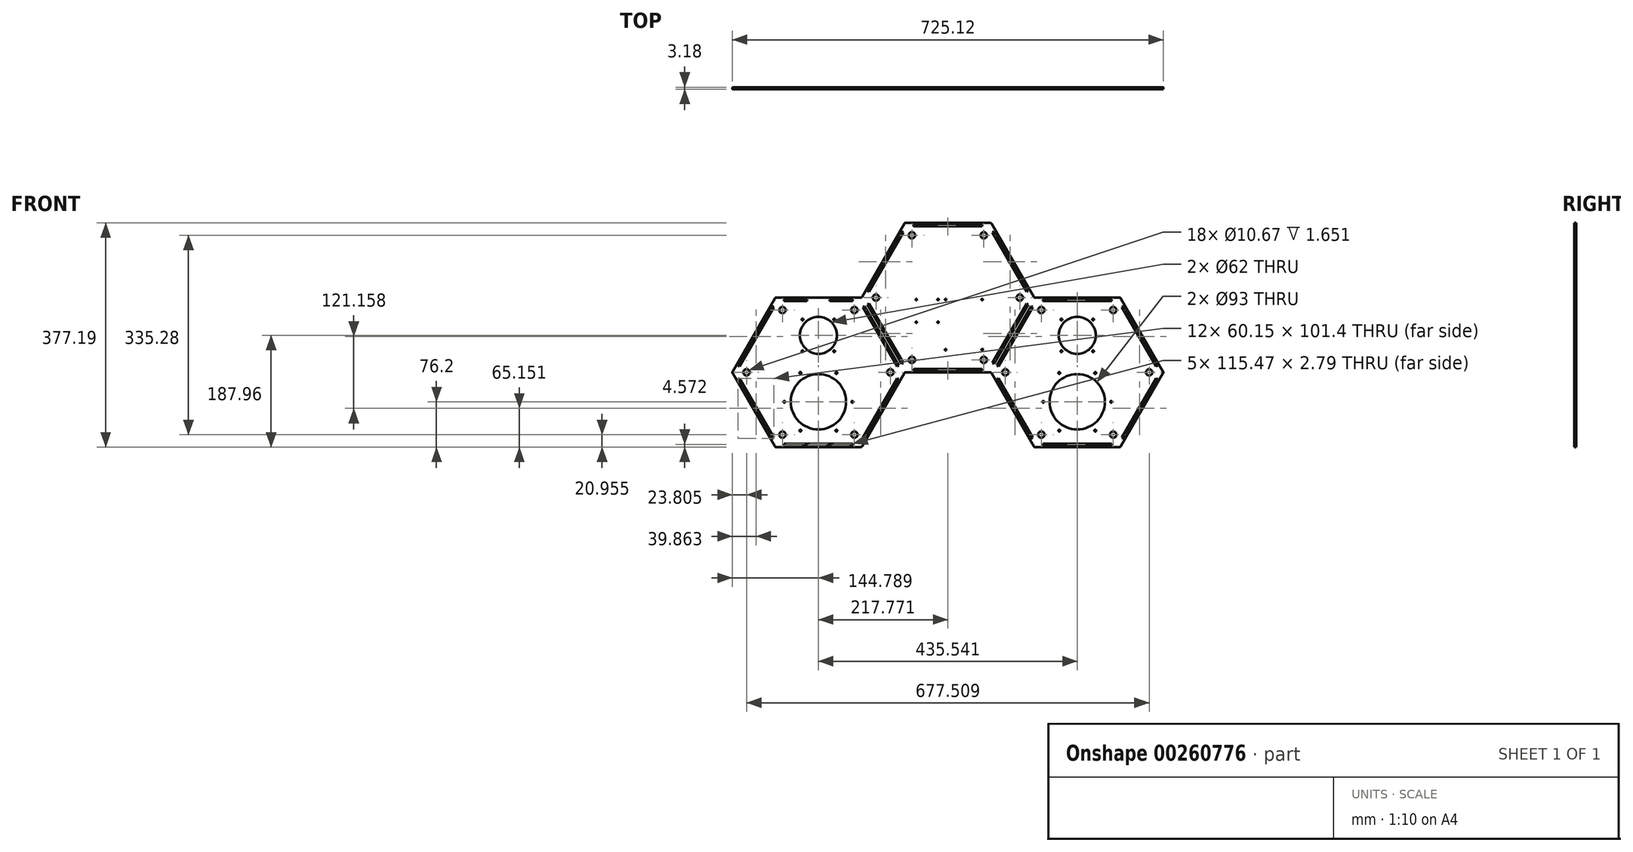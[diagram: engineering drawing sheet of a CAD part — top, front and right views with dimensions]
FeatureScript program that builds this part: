
annotation { "Feature Type Name" : "Feature", "Feature Type Description" : "" }
export const myFeature = defineFeature(function(context is Context, id is Id, definition is map)
    precondition{}
    {
        {
            var Q0;
            Q0=qCreatedBy(makeId("Front.planeOp"),FACE);
            var sketch = newSketch(context, id + "F0", { "sketchPlane" : qUnion([Q0])});
            skCircle(sketch, "E0.cCircle", {"center": v(0, 0) * mm, "radius": 125.73 * mm, "construction": true});
            skLineSegment(sketch, "E0.1", {"start": v(71.12, -125.73) * mm, "end": v(-71.12, -125.73) * mm});
            skLineSegment(sketch, "E0.3", {"start": v(-144.45, 1.27) * mm, "end": v(-73.32, 124.46) * mm});
            skLineSegment(sketch, "E0.4", {"start": v(-71.12, 125.73) * mm, "end": v(71.12, 125.73) * mm});
            skLineSegment(sketch, "E0.5", {"start": v(73.32, 124.46) * mm, "end": v(144.45, 1.27) * mm});
            skCircle(sketch, "E1.cCircle", {"center": v(-217.77, -125.73) * mm, "radius": 125.73 * mm, "construction": true});
            skLineSegment(sketch, "E1.0", {"start": v(-146.65, -251.46) * mm, "end": v(-288.9, -251.46) * mm});
            skLineSegment(sketch, "E1.1", {"start": v(-291.1, -250.19) * mm, "end": v(-362.22, -127) * mm});
            skLineSegment(sketch, "E1.2", {"start": v(-362.22, -124.46) * mm, "end": v(-291.1, -1.27) * mm});
            skLineSegment(sketch, "E1.3", {"start": v(-288.9, 0) * mm, "end": v(-146.65, 0) * mm});
            skLineSegment(sketch, "E1.5", {"start": v(-73.32, -127) * mm, "end": v(-144.45, -250.19) * mm});
            skPoint(sketch, "E1.0.midPoint", {"position": v(-217.77, -251.46) * mm});
            skCircle(sketch, "E2.cCircle", {"center": v(217.77, -125.73) * mm, "radius": 125.73 * mm, "construction": true});
            skLineSegment(sketch, "E2.0", {"start": v(362.22, -127) * mm, "end": v(291.1, -250.2) * mm});
            skLineSegment(sketch, "E2.1", {"start": v(288.9, -251.46) * mm, "end": v(146.65, -251.46) * mm});
            skLineSegment(sketch, "E2.2", {"start": v(144.45, -250.2) * mm, "end": v(73.32, -127) * mm});
            skLineSegment(sketch, "E2.4", {"start": v(146.65, 0) * mm, "end": v(288.9, 0) * mm});
            skLineSegment(sketch, "E2.5", {"start": v(291.1, -1.27) * mm, "end": v(362.22, -124.46) * mm});
            skPoint(sketch, "E2.0.midPoint", {"position": v(326.66, -188.6) * mm});
            skPoint(sketch, "E3.visualSharp", {"position": v(-72.6, 125.73) * mm});
            skArc(sketch, "E3.filletArc", {"start": v(-71.12, 125.73) * mm, "mid": v(-72.4, 125.39) * mm, "end": v(-73.32, 124.46) * mm});
            skPoint(sketch, "E4.visualSharp", {"position": v(72.6, 125.73) * mm});
            skArc(sketch, "E4.filletArc", {"start": v(73.32, 124.46) * mm, "mid": v(72.4, 125.39) * mm, "end": v(71.12, 125.73) * mm});
            skPoint(sketch, "E5.visualSharp", {"position": v(145.18, 0) * mm});
            skArc(sketch, "E5.filletArc", {"start": v(144.45, 1.27) * mm, "mid": v(145.38, 0.34) * mm, "end": v(146.65, 0) * mm});
            skPoint(sketch, "E6.visualSharp", {"position": v(290.36, 0) * mm});
            skArc(sketch, "E6.filletArc", {"start": v(291.1, -1.27) * mm, "mid": v(290.16, -0.34) * mm, "end": v(288.9, 0) * mm});
            skPoint(sketch, "E7.visualSharp", {"position": v(362.95, -125.73) * mm});
            skArc(sketch, "E7.filletArc", {"start": v(362.22, -127) * mm, "mid": v(362.56, -125.73) * mm, "end": v(362.22, -124.46) * mm});
            skPoint(sketch, "E8.visualSharp", {"position": v(290.36, -251.46) * mm});
            skArc(sketch, "E8.filletArc", {"start": v(288.9, -251.46) * mm, "mid": v(290.16, -251.12) * mm, "end": v(291.1, -250.2) * mm});
            skPoint(sketch, "E9.visualSharp", {"position": v(145.18, -251.46) * mm});
            skArc(sketch, "E9.filletArc", {"start": v(144.45, -250.2) * mm, "mid": v(145.38, -251.12) * mm, "end": v(146.65, -251.46) * mm});
            skPoint(sketch, "E10.visualSharp", {"position": v(72.6, -125.73) * mm});
            skArc(sketch, "E10.filletArc", {"start": v(73.32, -127) * mm, "mid": v(72.4, -126.07) * mm, "end": v(71.12, -125.73) * mm});
            skPoint(sketch, "E11.visualSharp", {"position": v(-72.6, -125.73) * mm});
            skArc(sketch, "E11.filletArc", {"start": v(-71.12, -125.73) * mm, "mid": v(-72.4, -126.07) * mm, "end": v(-73.32, -127) * mm});
            skPoint(sketch, "E12.visualSharp", {"position": v(-145.18, -251.46) * mm});
            skArc(sketch, "E12.filletArc", {"start": v(-146.65, -251.46) * mm, "mid": v(-145.38, -251.12) * mm, "end": v(-144.45, -250.19) * mm});
            skPoint(sketch, "E13.visualSharp", {"position": v(-290.36, -251.46) * mm});
            skArc(sketch, "E13.filletArc", {"start": v(-291.1, -250.19) * mm, "mid": v(-290.16, -251.12) * mm, "end": v(-288.9, -251.46) * mm});
            skPoint(sketch, "E14.visualSharp", {"position": v(-362.95, -125.73) * mm});
            skArc(sketch, "E14.filletArc", {"start": v(-362.22, -124.46) * mm, "mid": v(-362.56, -125.73) * mm, "end": v(-362.22, -127) * mm});
            skPoint(sketch, "E15.visualSharp", {"position": v(-290.36, 0) * mm});
            skArc(sketch, "E15.filletArc", {"start": v(-288.9, 0) * mm, "mid": v(-290.16, -0.34) * mm, "end": v(-291.1, -1.27) * mm});
            skPoint(sketch, "E16.visualSharp", {"position": v(-145.18, 0) * mm});
            skArc(sketch, "E16.filletArc", {"start": v(-146.65, 0) * mm, "mid": v(-145.38, 0.34) * mm, "end": v(-144.45, 1.27) * mm});
            skCircle(sketch, "E17.cCircle", {"center": v(-217.77, -125.73) * mm, "radius": 104.78 * mm, "construction": true});
            skLineSegment(sketch, "E17.0", {"start": v(-278.26, -20.95) * mm, "end": v(-157.28, -20.96) * mm, "construction": true});
            skLineSegment(sketch, "E17.1", {"start": v(-157.28, -20.95) * mm, "end": v(-96.79, -125.73) * mm, "construction": true});
            skLineSegment(sketch, "E17.2", {"start": v(-96.79, -125.73) * mm, "end": v(-157.28, -230.5) * mm, "construction": true});
            skLineSegment(sketch, "E17.3", {"start": v(-157.28, -230.5) * mm, "end": v(-278.26, -230.5) * mm, "construction": true});
            skLineSegment(sketch, "E17.4", {"start": v(-278.26, -230.5) * mm, "end": v(-338.75, -125.73) * mm, "construction": true});
            skLineSegment(sketch, "E17.5", {"start": v(-338.75, -125.73) * mm, "end": v(-278.26, -20.96) * mm, "construction": true});
            skPoint(sketch, "E17.0.midPoint", {"position": v(-217.77, -20.96) * mm});
            skCircle(sketch, "E18.cCircle", {"center": v(0, 0) * mm, "radius": 104.78 * mm, "construction": true});
            skLineSegment(sketch, "E18.0", {"start": v(60.5, 104.78) * mm, "end": v(120.98, 0) * mm, "construction": true});
            skLineSegment(sketch, "E18.1", {"start": v(120.98, 0) * mm, "end": v(60.5, -104.77) * mm, "construction": true});
            skLineSegment(sketch, "E18.2", {"start": v(60.5, -104.77) * mm, "end": v(-60.5, -104.78) * mm, "construction": true});
            skLineSegment(sketch, "E18.3", {"start": v(-60.5, -104.78) * mm, "end": v(-120.98, 0) * mm, "construction": true});
            skLineSegment(sketch, "E18.4", {"start": v(-120.98, 0) * mm, "end": v(-60.5, 104.78) * mm, "construction": true});
            skLineSegment(sketch, "E18.5", {"start": v(-60.5, 104.77) * mm, "end": v(60.5, 104.77) * mm, "construction": true});
            skPoint(sketch, "E18.0.midPoint", {"position": v(90.74, 52.39) * mm});
            skCircle(sketch, "E19.cCircle", {"center": v(217.77, -125.73) * mm, "radius": 104.78 * mm, "construction": true});
            skLineSegment(sketch, "E19.0", {"start": v(157.28, -20.96) * mm, "end": v(278.26, -20.96) * mm, "construction": true});
            skLineSegment(sketch, "E19.1", {"start": v(278.26, -20.96) * mm, "end": v(338.75, -125.73) * mm, "construction": true});
            skLineSegment(sketch, "E19.2", {"start": v(338.75, -125.73) * mm, "end": v(278.26, -230.5) * mm, "construction": true});
            skLineSegment(sketch, "E19.3", {"start": v(278.26, -230.5) * mm, "end": v(157.28, -230.5) * mm, "construction": true});
            skLineSegment(sketch, "E19.4", {"start": v(157.28, -230.5) * mm, "end": v(96.79, -125.73) * mm, "construction": true});
            skLineSegment(sketch, "E19.5", {"start": v(96.79, -125.73) * mm, "end": v(157.28, -20.96) * mm, "construction": true});
            skPoint(sketch, "E19.0.midPoint", {"position": v(217.77, -20.96) * mm});
            skCircle(sketch, "E20", {"center": v(-278.26, -20.96) * mm, "radius": 5.33 * mm});
            skCircle(sketch, "E21", {"center": v(-157.28, -20.95) * mm, "radius": 5.33 * mm});
            skCircle(sketch, "E22", {"center": v(-338.75, -125.73) * mm, "radius": 5.33 * mm});
            skCircle(sketch, "E23", {"center": v(-278.26, -230.5) * mm, "radius": 5.33 * mm});
            skCircle(sketch, "E24", {"center": v(-157.28, -230.5) * mm, "radius": 5.33 * mm});
            skCircle(sketch, "E25", {"center": v(-96.79, -125.73) * mm, "radius": 5.33 * mm});
            skCircle(sketch, "E26", {"center": v(-60.5, -104.78) * mm, "radius": 5.33 * mm});
            skCircle(sketch, "E27", {"center": v(-120.98, 0) * mm, "radius": 5.33 * mm});
            skCircle(sketch, "E28", {"center": v(-60.5, 104.77) * mm, "radius": 5.33 * mm});
            skCircle(sketch, "E29", {"center": v(60.5, 104.77) * mm, "radius": 5.33 * mm});
            skCircle(sketch, "E30", {"center": v(120.98, 0) * mm, "radius": 5.33 * mm});
            skCircle(sketch, "E31", {"center": v(60.5, -104.77) * mm, "radius": 5.33 * mm});
            skCircle(sketch, "E32", {"center": v(96.79, -125.73) * mm, "radius": 5.33 * mm});
            skCircle(sketch, "E33", {"center": v(157.28, -20.96) * mm, "radius": 5.33 * mm});
            skCircle(sketch, "E34", {"center": v(278.26, -20.96) * mm, "radius": 5.33 * mm});
            skCircle(sketch, "E35", {"center": v(338.75, -125.73) * mm, "radius": 5.33 * mm});
            skCircle(sketch, "E36", {"center": v(278.26, -230.5) * mm, "radius": 5.33 * mm});
            skCircle(sketch, "E37", {"center": v(157.28, -230.5) * mm, "radius": 5.33 * mm});
            skSolve(sketch);
        }
        {
            var Q0;
            Q0=makeQuery(id+"F0.imprint","IMPRINT",FACE,{"disambiguationData":[TD([[makeQuery(id+"F0.imprint","IMPRINT",EDGE,{"derivedFrom":sQuery(id+"F0.wireOp",EDGE,"E0.1")}),-1.0]])]});
            extrude(context, id + "F1", {"entities" : qUnion([Q0]), "depth" : 3.17 * mm});
        }
        {
            var Q0;
            Q0=makeQuery(id+"F0.imprint","IMPRINT",FACE,{"disambiguationData":[TD([[makeQuery(id+"F0.imprint","IMPRINT",EDGE,{"derivedFrom":sQuery(id+"F0.wireOp",EDGE,"E30")}),1.0]])]});
            var Q1;
            Q1=makeQuery(id+"F0.imprint","IMPRINT",FACE,{"disambiguationData":[TD([[makeQuery(id+"F0.imprint","IMPRINT",EDGE,{"derivedFrom":sQuery(id+"F0.wireOp",EDGE,"E33")}),1.0]])]});
            var Q2;
            Q2=makeQuery(id+"F0.imprint","IMPRINT",FACE,{"disambiguationData":[TD([[makeQuery(id+"F0.imprint","IMPRINT",EDGE,{"derivedFrom":sQuery(id+"F0.wireOp",EDGE,"E34")}),1.0]])]});
            var Q3;
            Q3=makeQuery(id+"F0.imprint","IMPRINT",FACE,{"disambiguationData":[TD([[makeQuery(id+"F0.imprint","IMPRINT",EDGE,{"derivedFrom":sQuery(id+"F0.wireOp",EDGE,"E35")}),1.0]])]});
            var Q4;
            Q4=makeQuery(id+"F0.imprint","IMPRINT",FACE,{"disambiguationData":[TD([[makeQuery(id+"F0.imprint","IMPRINT",EDGE,{"derivedFrom":sQuery(id+"F0.wireOp",EDGE,"E36")}),1.0]])]});
            var Q5;
            Q5=makeQuery(id+"F0.imprint","IMPRINT",FACE,{"disambiguationData":[TD([[makeQuery(id+"F0.imprint","IMPRINT",EDGE,{"derivedFrom":sQuery(id+"F0.wireOp",EDGE,"E37")}),1.0]])]});
            var Q6;
            Q6=makeQuery(id+"F0.imprint","IMPRINT",FACE,{"disambiguationData":[TD([[makeQuery(id+"F0.imprint","IMPRINT",EDGE,{"derivedFrom":sQuery(id+"F0.wireOp",EDGE,"E32")}),1.0]])]});
            var Q7;
            Q7=makeQuery(id+"F0.imprint","IMPRINT",FACE,{"disambiguationData":[TD([[makeQuery(id+"F0.imprint","IMPRINT",EDGE,{"derivedFrom":sQuery(id+"F0.wireOp",EDGE,"E31")}),1.0]])]});
            var Q8;
            Q8=makeQuery(id+"F0.imprint","IMPRINT",FACE,{"disambiguationData":[TD([[makeQuery(id+"F0.imprint","IMPRINT",EDGE,{"derivedFrom":sQuery(id+"F0.wireOp",EDGE,"E26")}),1.0]])]});
            var Q9;
            Q9=makeQuery(id+"F0.imprint","IMPRINT",FACE,{"disambiguationData":[TD([[makeQuery(id+"F0.imprint","IMPRINT",EDGE,{"derivedFrom":sQuery(id+"F0.wireOp",EDGE,"E25")}),1.0]])]});
            var Q10;
            Q10=makeQuery(id+"F0.imprint","IMPRINT",FACE,{"disambiguationData":[TD([[makeQuery(id+"F0.imprint","IMPRINT",EDGE,{"derivedFrom":sQuery(id+"F0.wireOp",EDGE,"E24")}),1.0]])]});
            var Q11;
            Q11=makeQuery(id+"F0.imprint","IMPRINT",FACE,{"disambiguationData":[TD([[makeQuery(id+"F0.imprint","IMPRINT",EDGE,{"derivedFrom":sQuery(id+"F0.wireOp",EDGE,"E23")}),1.0]])]});
            var Q12;
            Q12=makeQuery(id+"F0.imprint","IMPRINT",FACE,{"disambiguationData":[TD([[makeQuery(id+"F0.imprint","IMPRINT",EDGE,{"derivedFrom":sQuery(id+"F0.wireOp",EDGE,"E22")}),1.0]])]});
            var Q13;
            Q13=makeQuery(id+"F0.imprint","IMPRINT",FACE,{"disambiguationData":[TD([[makeQuery(id+"F0.imprint","IMPRINT",EDGE,{"derivedFrom":sQuery(id+"F0.wireOp",EDGE,"E20")}),1.0]])]});
            var Q14;
            Q14=makeQuery(id+"F0.imprint","IMPRINT",FACE,{"disambiguationData":[TD([[makeQuery(id+"F0.imprint","IMPRINT",EDGE,{"derivedFrom":sQuery(id+"F0.wireOp",EDGE,"E21")}),1.0]])]});
            var Q15;
            Q15=makeQuery(id+"F0.imprint","IMPRINT",FACE,{"disambiguationData":[TD([[makeQuery(id+"F0.imprint","IMPRINT",EDGE,{"derivedFrom":sQuery(id+"F0.wireOp",EDGE,"E27")}),1.0]])]});
            var Q16;
            Q16=makeQuery(id+"F0.imprint","IMPRINT",FACE,{"disambiguationData":[TD([[makeQuery(id+"F0.imprint","IMPRINT",EDGE,{"derivedFrom":sQuery(id+"F0.wireOp",EDGE,"E28")}),1.0]])]});
            var Q17;
            Q17=makeQuery(id+"F0.imprint","IMPRINT",FACE,{"disambiguationData":[TD([[makeQuery(id+"F0.imprint","IMPRINT",EDGE,{"derivedFrom":sQuery(id+"F0.wireOp",EDGE,"E29")}),1.0]])]});
            extrude(context, id + "F2", {"entities" : qUnion([Q0, Q1, Q2, Q3, Q4, Q5, Q6, Q7, Q8, Q9, Q10, Q11, Q12, Q13, Q14, Q15, Q16, Q17]), "operationType" : NewBodyOperationType.ADD, "depth" : 1.52 * mm});
        }
        {
            var Q0;
            Q0=makeQuery(id+"F1.opExtrude","CAP_FACE",FACE,{"disambiguationData":[OSD([sQuery(id+"F0.wireOp",EDGE,"E0.1"),sQuery(id+"F0.wireOp",EDGE,"E0.3"),sQuery(id+"F0.wireOp",EDGE,"E0.4"),sQuery(id+"F0.wireOp",EDGE,"E0.5"),sQuery(id+"F0.wireOp",EDGE,"E1.0"),sQuery(id+"F0.wireOp",EDGE,"E1.1"),sQuery(id+"F0.wireOp",EDGE,"E1.2"),sQuery(id+"F0.wireOp",EDGE,"E1.3"),sQuery(id+"F0.wireOp",EDGE,"E1.5"),sQuery(id+"F0.wireOp",EDGE,"E2.0"),sQuery(id+"F0.wireOp",EDGE,"E2.1"),sQuery(id+"F0.wireOp",EDGE,"E2.2"),sQuery(id+"F0.wireOp",EDGE,"E2.4"),sQuery(id+"F0.wireOp",EDGE,"E2.5"),sQuery(id+"F0.wireOp",EDGE,"E3.filletArc"),sQuery(id+"F0.wireOp",EDGE,"E4.filletArc"),sQuery(id+"F0.wireOp",EDGE,"E5.filletArc"),sQuery(id+"F0.wireOp",EDGE,"E6.filletArc"),sQuery(id+"F0.wireOp",EDGE,"E7.filletArc"),sQuery(id+"F0.wireOp",EDGE,"E8.filletArc"),sQuery(id+"F0.wireOp",EDGE,"E9.filletArc"),sQuery(id+"F0.wireOp",EDGE,"E10.filletArc"),sQuery(id+"F0.wireOp",EDGE,"E11.filletArc"),sQuery(id+"F0.wireOp",EDGE,"E12.filletArc"),sQuery(id+"F0.wireOp",EDGE,"E13.filletArc"),sQuery(id+"F0.wireOp",EDGE,"E14.filletArc"),sQuery(id+"F0.wireOp",EDGE,"E15.filletArc"),sQuery(id+"F0.wireOp",EDGE,"E16.filletArc"),sQuery(id+"F0.wireOp",EDGE,"E20"),sQuery(id+"F0.wireOp",EDGE,"E21"),sQuery(id+"F0.wireOp",EDGE,"E22"),sQuery(id+"F0.wireOp",EDGE,"E23"),sQuery(id+"F0.wireOp",EDGE,"E24"),sQuery(id+"F0.wireOp",EDGE,"E25"),sQuery(id+"F0.wireOp",EDGE,"E26"),sQuery(id+"F0.wireOp",EDGE,"E27"),sQuery(id+"F0.wireOp",EDGE,"E28"),sQuery(id+"F0.wireOp",EDGE,"E29"),sQuery(id+"F0.wireOp",EDGE,"E30"),sQuery(id+"F0.wireOp",EDGE,"E31"),sQuery(id+"F0.wireOp",EDGE,"E32"),sQuery(id+"F0.wireOp",EDGE,"E33"),sQuery(id+"F0.wireOp",EDGE,"E34"),sQuery(id+"F0.wireOp",EDGE,"E35"),sQuery(id+"F0.wireOp",EDGE,"E36"),sQuery(id+"F0.wireOp",EDGE,"E37")])],"isStart":false});
            var sketch = newSketch(context, id + "F3", { "sketchPlane" : qUnion([Q0])});
            skPoint(sketch, "E38", {"position": v(-217.77, -127) * mm});
            skCircle(sketch, "E39", {"center": v(-217.77, -63.5) * mm, "radius": 31 * mm});
            skCircle(sketch, "E40", {"center": v(-217.77, -175.26) * mm, "radius": 46.5 * mm});
            skLineSegment(sketch, "E41", {"start": v(-295.75, -175.26) * mm, "end": v(-133.33, -175.26) * mm, "construction": true});
            skCircle(sketch, "E42", {"center": v(-217.77, -175.26) * mm, "radius": 61.65 * mm, "construction": true});
            skCircle(sketch, "E43", {"center": v(-217.77, -175.26) * mm, "radius": 57.15 * mm, "construction": true});
            skCircle(sketch, "E44", {"center": v(-160.62, -175.26) * mm, "radius": 1.52 * mm});
            skLineSegment(sketch, "E45", {"start": v(-217.77, -175.26) * mm, "end": v(-217.77, -149.19) * mm, "construction": true});
            skLineSegment(sketch, "E46", {"start": v(-217.77, -175.26) * mm, "end": v(-187.49, -126.8) * mm, "construction": true});
            skLineSegment(sketch, "E47", {"start": v(-217.77, -175.26) * mm, "end": v(-187.49, -223.73) * mm, "construction": true});
            skCircle(sketch, "E48", {"center": v(-187.49, -126.8) * mm, "radius": 1.52 * mm});
            skCircle(sketch, "E49", {"center": v(-187.49, -223.73) * mm, "radius": 1.52 * mm});
            skCircle(sketch, "E50.MirrorC", {"center": v(-248.06, -126.8) * mm, "radius": 1.52 * mm});
            skCircle(sketch, "E51.MirrorC", {"center": v(-248.06, -223.73) * mm, "radius": 1.52 * mm});
            skCircle(sketch, "E52.MirrorC", {"center": v(-274.92, -175.26) * mm, "radius": 1.52 * mm});
            skCircle(sketch, "E53", {"center": v(-217.77, -63.5) * mm, "radius": 37.72 * mm, "construction": true});
            skLineSegment(sketch, "E54", {"start": v(-217.77, -63.5) * mm, "end": v(-244.44, -36.83) * mm, "construction": true});
            skCircle(sketch, "E55", {"center": v(-244.44, -36.83) * mm, "radius": 1.52 * mm});
            skCircle(sketch, "E56", {"center": v(-244.44, -90.17) * mm, "radius": 1.52 * mm});
            skCircle(sketch, "E57", {"center": v(-191.1, -90.17) * mm, "radius": 1.52 * mm});
            skCircle(sketch, "E58", {"center": v(-191.1, -36.83) * mm, "radius": 1.52 * mm});
            skLineSegment(sketch, "E59", {"start": v(-244.44, -36.83) * mm, "end": v(-191.1, -36.83) * mm, "construction": true});
            skCircle(sketch, "E60.MirrorC", {"center": v(160.62, -175.26) * mm, "radius": 1.52 * mm});
            skCircle(sketch, "E61.MirrorC", {"center": v(187.49, -223.73) * mm, "radius": 1.52 * mm});
            skCircle(sketch, "E62.MirrorC", {"center": v(248.06, -223.73) * mm, "radius": 1.52 * mm});
            skCircle(sketch, "E63.MirrorC", {"center": v(274.92, -175.26) * mm, "radius": 1.52 * mm});
            skCircle(sketch, "E64.MirrorC", {"center": v(187.49, -126.8) * mm, "radius": 1.52 * mm});
            skCircle(sketch, "E65.MirrorC", {"center": v(248.06, -126.8) * mm, "radius": 1.52 * mm});
            skCircle(sketch, "E66.MirrorC", {"center": v(217.77, -175.26) * mm, "radius": 46.5 * mm});
            skCircle(sketch, "E67.MirrorC", {"center": v(244.44, -90.17) * mm, "radius": 1.52 * mm});
            skCircle(sketch, "E68.MirrorC", {"center": v(191.1, -90.17) * mm, "radius": 1.52 * mm});
            skCircle(sketch, "E69.MirrorC", {"center": v(191.1, -36.83) * mm, "radius": 1.52 * mm});
            skCircle(sketch, "E70.MirrorC", {"center": v(217.77, -63.5) * mm, "radius": 31 * mm});
            skCircle(sketch, "E71.MirrorC", {"center": v(244.44, -36.83) * mm, "radius": 1.52 * mm});
            skSolve(sketch);
        }
        {
            var Q0;
            Q0=qSketchRegion(id+"F3",true);
            extrude(context, id + "F4", {"entities" : qUnion([Q0]), "operationType" : NewBodyOperationType.REMOVE, "endBound" : BoundingType.THROUGH_ALL, "oppositeDirection" : true, "depth" : 25.4 * mm});
        }
        {
            var Q0;
            Q0=makeQuery(id+"F1.opExtrude","CAP_FACE",FACE,{"disambiguationData":[OSD([sQuery(id+"F0.wireOp",EDGE,"E0.1"),sQuery(id+"F0.wireOp",EDGE,"E0.3"),sQuery(id+"F0.wireOp",EDGE,"E0.4"),sQuery(id+"F0.wireOp",EDGE,"E0.5"),sQuery(id+"F0.wireOp",EDGE,"E1.0"),sQuery(id+"F0.wireOp",EDGE,"E1.1"),sQuery(id+"F0.wireOp",EDGE,"E1.2"),sQuery(id+"F0.wireOp",EDGE,"E1.3"),sQuery(id+"F0.wireOp",EDGE,"E1.5"),sQuery(id+"F0.wireOp",EDGE,"E2.0"),sQuery(id+"F0.wireOp",EDGE,"E2.1"),sQuery(id+"F0.wireOp",EDGE,"E2.2"),sQuery(id+"F0.wireOp",EDGE,"E2.4"),sQuery(id+"F0.wireOp",EDGE,"E2.5"),sQuery(id+"F0.wireOp",EDGE,"E3.filletArc"),sQuery(id+"F0.wireOp",EDGE,"E4.filletArc"),sQuery(id+"F0.wireOp",EDGE,"E5.filletArc"),sQuery(id+"F0.wireOp",EDGE,"E6.filletArc"),sQuery(id+"F0.wireOp",EDGE,"E7.filletArc"),sQuery(id+"F0.wireOp",EDGE,"E8.filletArc"),sQuery(id+"F0.wireOp",EDGE,"E9.filletArc"),sQuery(id+"F0.wireOp",EDGE,"E10.filletArc"),sQuery(id+"F0.wireOp",EDGE,"E11.filletArc"),sQuery(id+"F0.wireOp",EDGE,"E12.filletArc"),sQuery(id+"F0.wireOp",EDGE,"E13.filletArc"),sQuery(id+"F0.wireOp",EDGE,"E14.filletArc"),sQuery(id+"F0.wireOp",EDGE,"E15.filletArc"),sQuery(id+"F0.wireOp",EDGE,"E16.filletArc"),sQuery(id+"F0.wireOp",EDGE,"E20"),sQuery(id+"F0.wireOp",EDGE,"E21"),sQuery(id+"F0.wireOp",EDGE,"E22"),sQuery(id+"F0.wireOp",EDGE,"E23"),sQuery(id+"F0.wireOp",EDGE,"E24"),sQuery(id+"F0.wireOp",EDGE,"E25"),sQuery(id+"F0.wireOp",EDGE,"E26"),sQuery(id+"F0.wireOp",EDGE,"E27"),sQuery(id+"F0.wireOp",EDGE,"E28"),sQuery(id+"F0.wireOp",EDGE,"E29"),sQuery(id+"F0.wireOp",EDGE,"E30"),sQuery(id+"F0.wireOp",EDGE,"E31"),sQuery(id+"F0.wireOp",EDGE,"E32"),sQuery(id+"F0.wireOp",EDGE,"E33"),sQuery(id+"F0.wireOp",EDGE,"E34"),sQuery(id+"F0.wireOp",EDGE,"E35"),sQuery(id+"F0.wireOp",EDGE,"E36"),sQuery(id+"F0.wireOp",EDGE,"E37")])],"isStart":false});
            var sketch = newSketch(context, id + "F5", { "sketchPlane" : qUnion([Q0])});
            skPoint(sketch, "E72", {"position": v(-217.77, -125.73) * mm});
            skCircle(sketch, "E73.cCircle", {"center": v(-217.77, -125.73) * mm, "radius": 125.73 * mm, "construction": true});
            skLineSegment(sketch, "E73.0", {"start": v(-275.7, 0) * mm, "end": v(-159.85, 0) * mm, "construction": true});
            skLineSegment(sketch, "E73.1", {"start": v(-137.85, -12.7) * mm, "end": v(-79.92, -113.03) * mm, "construction": true});
            skLineSegment(sketch, "E73.2", {"start": v(-79.92, -138.43) * mm, "end": v(-137.85, -238.76) * mm, "construction": true});
            skLineSegment(sketch, "E73.3", {"start": v(-159.85, -251.46) * mm, "end": v(-275.7, -251.46) * mm, "construction": true});
            skLineSegment(sketch, "E73.4", {"start": v(-297.7, -238.76) * mm, "end": v(-355.62, -138.43) * mm, "construction": true});
            skLineSegment(sketch, "E73.5", {"start": v(-355.62, -113.03) * mm, "end": v(-297.7, -12.7) * mm, "construction": true});
            skPoint(sketch, "E73.0.midPoint", {"position": v(-217.77, 0) * mm});
            skPoint(sketch, "E74.visualSharp", {"position": v(-290.36, 0) * mm});
            skArc(sketch, "E74.filletArc", {"start": v(-275.7, 0) * mm, "mid": v(-288.4, -3.4) * mm, "end": v(-297.7, -12.7) * mm, "construction": true});
            skPoint(sketch, "E75.visualSharp", {"position": v(-145.18, 0) * mm});
            skArc(sketch, "E75.filletArc", {"start": v(-137.85, -12.7) * mm, "mid": v(-147.15, -3.4) * mm, "end": v(-159.85, 0) * mm, "construction": true});
            skPoint(sketch, "E76.visualSharp", {"position": v(-72.6, -125.73) * mm});
            skArc(sketch, "E76.filletArc", {"start": v(-79.92, -138.43) * mm, "mid": v(-76.52, -125.73) * mm, "end": v(-79.92, -113.03) * mm, "construction": true});
            skPoint(sketch, "E77.visualSharp", {"position": v(-145.18, -251.46) * mm});
            skArc(sketch, "E77.filletArc", {"start": v(-159.85, -251.46) * mm, "mid": v(-147.15, -248.06) * mm, "end": v(-137.85, -238.76) * mm, "construction": true});
            skPoint(sketch, "E78.visualSharp", {"position": v(-290.36, -251.46) * mm});
            skArc(sketch, "E78.filletArc", {"start": v(-297.7, -238.76) * mm, "mid": v(-288.4, -248.06) * mm, "end": v(-275.7, -251.46) * mm, "construction": true});
            skPoint(sketch, "E79.visualSharp", {"position": v(-362.95, -125.73) * mm});
            skArc(sketch, "E79.filletArc", {"start": v(-355.62, -113.03) * mm, "mid": v(-359.02, -125.73) * mm, "end": v(-355.62, -138.43) * mm, "construction": true});
            skLineSegment(sketch, "E80.bottom", {"start": v(-275.5, -5.97) * mm, "end": v(-160.04, -5.97) * mm});
            skLineSegment(sketch, "E80.top", {"start": v(-275.5, -3.18) * mm, "end": v(-160.04, -3.18) * mm});
            skLineSegment(sketch, "E80.left", {"start": v(-275.5, -3.18) * mm, "end": v(-275.5, -5.97) * mm});
            skLineSegment(sketch, "E80.right", {"start": v(-160.04, -3.18) * mm, "end": v(-160.04, -5.97) * mm});
            skLineSegment(sketch, "E81.1.0", {"start": v(-352.77, -114.45) * mm, "end": v(-295.04, -14.45) * mm});
            skLineSegment(sketch, "E81.1.1", {"start": v(-352.77, -114.45) * mm, "end": v(-350.35, -115.85) * mm});
            skLineSegment(sketch, "E81.1.2", {"start": v(-350.35, -115.85) * mm, "end": v(-292.62, -15.85) * mm});
            skLineSegment(sketch, "E81.1.3", {"start": v(-295.04, -14.45) * mm, "end": v(-292.62, -15.85) * mm});
            skLineSegment(sketch, "E81.2.0", {"start": v(-295.04, -237) * mm, "end": v(-352.77, -137) * mm});
            skLineSegment(sketch, "E81.2.1", {"start": v(-295.04, -237) * mm, "end": v(-292.62, -235.61) * mm});
            skLineSegment(sketch, "E81.2.2", {"start": v(-292.62, -235.61) * mm, "end": v(-350.35, -135.61) * mm});
            skLineSegment(sketch, "E81.2.3", {"start": v(-352.77, -137) * mm, "end": v(-350.35, -135.61) * mm});
            skLineSegment(sketch, "E81.3.0", {"start": v(-160.04, -248.28) * mm, "end": v(-275.5, -248.28) * mm});
            skLineSegment(sketch, "E81.3.1", {"start": v(-160.04, -248.28) * mm, "end": v(-160.04, -245.5) * mm});
            skLineSegment(sketch, "E81.3.2", {"start": v(-160.04, -245.5) * mm, "end": v(-275.5, -245.5) * mm});
            skLineSegment(sketch, "E81.3.3", {"start": v(-275.5, -248.28) * mm, "end": v(-275.5, -245.5) * mm});
            skLineSegment(sketch, "E81.4.0", {"start": v(-82.77, -137) * mm, "end": v(-140.5, -237) * mm});
            skLineSegment(sketch, "E81.4.1", {"start": v(-82.77, -137) * mm, "end": v(-85.19, -135.61) * mm});
            skLineSegment(sketch, "E81.4.2", {"start": v(-85.19, -135.61) * mm, "end": v(-142.92, -235.61) * mm});
            skLineSegment(sketch, "E81.4.3", {"start": v(-140.5, -237) * mm, "end": v(-142.92, -235.61) * mm});
            skLineSegment(sketch, "E81.5.0", {"start": v(-140.5, -14.45) * mm, "end": v(-82.77, -114.45) * mm});
            skLineSegment(sketch, "E81.5.1", {"start": v(-140.5, -14.45) * mm, "end": v(-142.92, -15.85) * mm});
            skLineSegment(sketch, "E81.5.2", {"start": v(-142.92, -15.85) * mm, "end": v(-85.19, -115.85) * mm});
            skLineSegment(sketch, "E81.5.3", {"start": v(-82.77, -114.45) * mm, "end": v(-85.19, -115.85) * mm});
            skLineSegment(sketch, "E82.MirrorCS", {"start": v(140.5, -14.45) * mm, "end": v(142.92, -15.85) * mm});
            skLineSegment(sketch, "E83.MirrorCS", {"start": v(140.5, -14.45) * mm, "end": v(82.77, -114.45) * mm});
            skLineSegment(sketch, "E84.MirrorCS", {"start": v(142.92, -15.85) * mm, "end": v(85.19, -115.85) * mm});
            skLineSegment(sketch, "E85.MirrorCS", {"start": v(82.77, -114.45) * mm, "end": v(85.19, -115.85) * mm});
            skLineSegment(sketch, "E86.MirrorCS", {"start": v(82.77, -137) * mm, "end": v(85.19, -135.61) * mm});
            skLineSegment(sketch, "E87.MirrorCS", {"start": v(85.19, -135.61) * mm, "end": v(142.92, -235.61) * mm});
            skLineSegment(sketch, "E88.MirrorCS", {"start": v(82.77, -137) * mm, "end": v(140.5, -237) * mm});
            skLineSegment(sketch, "E89.MirrorCS", {"start": v(140.5, -237) * mm, "end": v(142.92, -235.61) * mm});
            skLineSegment(sketch, "E90.MirrorCS", {"start": v(160.04, -248.28) * mm, "end": v(160.04, -245.5) * mm});
            skLineSegment(sketch, "E91.MirrorCS", {"start": v(160.04, -248.28) * mm, "end": v(275.5, -248.28) * mm});
            skLineSegment(sketch, "E92.MirrorCS", {"start": v(160.04, -245.5) * mm, "end": v(275.5, -245.5) * mm});
            skLineSegment(sketch, "E93.MirrorCS", {"start": v(275.5, -248.28) * mm, "end": v(275.5, -245.5) * mm});
            skLineSegment(sketch, "E94.MirrorCS", {"start": v(295.04, -237) * mm, "end": v(292.62, -235.61) * mm});
            skLineSegment(sketch, "E95.MirrorCS", {"start": v(295.04, -237) * mm, "end": v(352.77, -137) * mm});
            skLineSegment(sketch, "E96.MirrorCS", {"start": v(292.62, -235.61) * mm, "end": v(350.35, -135.61) * mm});
            skLineSegment(sketch, "E97.MirrorCS", {"start": v(352.77, -137) * mm, "end": v(350.35, -135.61) * mm});
            skLineSegment(sketch, "E98.MirrorCS", {"start": v(352.77, -114.45) * mm, "end": v(350.35, -115.85) * mm});
            skLineSegment(sketch, "E99.MirrorCS", {"start": v(350.35, -115.85) * mm, "end": v(292.62, -15.85) * mm});
            skLineSegment(sketch, "E100.MirrorCS", {"start": v(352.77, -114.45) * mm, "end": v(295.04, -14.45) * mm});
            skLineSegment(sketch, "E101.MirrorCS", {"start": v(295.04, -14.45) * mm, "end": v(292.62, -15.85) * mm});
            skLineSegment(sketch, "E102.MirrorCS", {"start": v(275.5, -3.18) * mm, "end": v(275.5, -5.97) * mm});
            skLineSegment(sketch, "E103.MirrorCS", {"start": v(275.5, -5.97) * mm, "end": v(160.04, -5.97) * mm});
            skLineSegment(sketch, "E104.MirrorCS", {"start": v(275.5, -3.18) * mm, "end": v(160.04, -3.18) * mm});
            skLineSegment(sketch, "E105.MirrorCS", {"start": v(160.04, -3.18) * mm, "end": v(160.04, -5.97) * mm});
            skLineSegment(sketch, "E106.MirrorCS", {"start": v(57.74, -122.55) * mm, "end": v(57.74, -119.76) * mm});
            skLineSegment(sketch, "E107.MirrorCS", {"start": v(-57.74, -122.55) * mm, "end": v(57.74, -122.55) * mm});
            skLineSegment(sketch, "E108.MirrorCS", {"start": v(-57.74, -119.76) * mm, "end": v(57.74, -119.76) * mm});
            skLineSegment(sketch, "E109.MirrorCS", {"start": v(-57.74, -122.55) * mm, "end": v(-57.74, -119.76) * mm});
            skLineSegment(sketch, "E110.MirrorCS", {"start": v(-77.27, -111.28) * mm, "end": v(-74.85, -109.88) * mm});
            skLineSegment(sketch, "E111.MirrorCS", {"start": v(-132.58, -9.88) * mm, "end": v(-74.85, -109.88) * mm});
            skLineSegment(sketch, "E112.MirrorCS", {"start": v(-135, -11.28) * mm, "end": v(-77.27, -111.28) * mm});
            skLineSegment(sketch, "E113.MirrorCS", {"start": v(-135, -11.28) * mm, "end": v(-132.58, -9.88) * mm});
            skLineSegment(sketch, "E114.MirrorCS", {"start": v(-135, 11.28) * mm, "end": v(-132.58, 9.88) * mm});
            skLineSegment(sketch, "E115.MirrorCS", {"start": v(-74.85, 109.88) * mm, "end": v(-132.58, 9.88) * mm});
            skLineSegment(sketch, "E116.MirrorCS", {"start": v(-77.27, 111.28) * mm, "end": v(-135, 11.28) * mm});
            skLineSegment(sketch, "E117.MirrorCS", {"start": v(-77.27, 111.28) * mm, "end": v(-74.85, 109.88) * mm});
            skLineSegment(sketch, "E118.MirrorCS", {"start": v(-57.74, 122.55) * mm, "end": v(-57.74, 119.76) * mm});
            skLineSegment(sketch, "E119.MirrorCS", {"start": v(57.74, 119.76) * mm, "end": v(-57.74, 119.76) * mm});
            skLineSegment(sketch, "E120.MirrorCS", {"start": v(57.74, 122.56) * mm, "end": v(-57.74, 122.56) * mm});
            skLineSegment(sketch, "E121.MirrorCS", {"start": v(57.74, 122.56) * mm, "end": v(57.74, 119.76) * mm});
            skLineSegment(sketch, "E122.MirrorCS", {"start": v(77.27, 111.28) * mm, "end": v(74.85, 109.88) * mm});
            skLineSegment(sketch, "E123.MirrorCS", {"start": v(132.58, 9.88) * mm, "end": v(74.85, 109.88) * mm});
            skLineSegment(sketch, "E124.MirrorCS", {"start": v(135, 11.28) * mm, "end": v(77.27, 111.28) * mm});
            skLineSegment(sketch, "E125.MirrorCS", {"start": v(135, 11.28) * mm, "end": v(132.58, 9.88) * mm});
            skLineSegment(sketch, "E126.MirrorCS", {"start": v(135, -11.28) * mm, "end": v(132.58, -9.88) * mm});
            skLineSegment(sketch, "E127.MirrorCS", {"start": v(74.85, -109.88) * mm, "end": v(132.58, -9.88) * mm});
            skLineSegment(sketch, "E128.MirrorCS", {"start": v(77.27, -111.28) * mm, "end": v(74.85, -109.88) * mm});
            skLineSegment(sketch, "E129.MirrorCS", {"start": v(77.27, -111.28) * mm, "end": v(135, -11.28) * mm});
            skSolve(sketch);
        }
        {
            var Q0;
            Q0=qSketchRegion(id+"F5",true);
            extrude(context, id + "F6", {"entities" : qUnion([Q0]), "operationType" : NewBodyOperationType.REMOVE, "endBound" : BoundingType.THROUGH_ALL, "oppositeDirection" : true, "depth" : 25.4 * mm});
        }
        {
            var Q0;
            {var subQ0=sQuery(id+"F0.wireOp",EDGE,"E25");var subQ1=sQuery(id+"F0.wireOp",EDGE,"E20");var subQ2=sQuery(id+"F0.wireOp",EDGE,"E21");var subQ3=sQuery(id+"F0.wireOp",EDGE,"E22");var subQ4=sQuery(id+"F0.wireOp",EDGE,"E23");var subQ5=sQuery(id+"F0.wireOp",EDGE,"E24");Q0=makeQuery(id+"F0aKffUkCtTZm95_1.boolean.opBoolean","SPLIT",FACE,{"disambiguationData":[TD([makeQuery(id+"F1.opExtrude","SWEPT_FACE",FACE,{"disambiguationData":[OSD([subQ1])]})])],"derivedFrom":makeQuery(id+"F1.opExtrude","CAP_FACE",FACE,{"disambiguationData":[OSD([sQuery(id+"F0.wireOp",EDGE,"E0.1"),sQuery(id+"F0.wireOp",EDGE,"E0.3"),sQuery(id+"F0.wireOp",EDGE,"E0.4"),sQuery(id+"F0.wireOp",EDGE,"E0.5"),sQuery(id+"F0.wireOp",EDGE,"E1.0"),sQuery(id+"F0.wireOp",EDGE,"E1.1"),sQuery(id+"F0.wireOp",EDGE,"E1.2"),sQuery(id+"F0.wireOp",EDGE,"E1.3"),sQuery(id+"F0.wireOp",EDGE,"E1.5"),sQuery(id+"F0.wireOp",EDGE,"E2.0"),sQuery(id+"F0.wireOp",EDGE,"E2.1"),sQuery(id+"F0.wireOp",EDGE,"E2.2"),sQuery(id+"F0.wireOp",EDGE,"E2.4"),sQuery(id+"F0.wireOp",EDGE,"E2.5"),sQuery(id+"F0.wireOp",EDGE,"E3.filletArc"),sQuery(id+"F0.wireOp",EDGE,"E4.filletArc"),sQuery(id+"F0.wireOp",EDGE,"E5.filletArc"),sQuery(id+"F0.wireOp",EDGE,"E6.filletArc"),sQuery(id+"F0.wireOp",EDGE,"E7.filletArc"),sQuery(id+"F0.wireOp",EDGE,"E8.filletArc"),sQuery(id+"F0.wireOp",EDGE,"E9.filletArc"),sQuery(id+"F0.wireOp",EDGE,"E10.filletArc"),sQuery(id+"F0.wireOp",EDGE,"E11.filletArc"),sQuery(id+"F0.wireOp",EDGE,"E12.filletArc"),sQuery(id+"F0.wireOp",EDGE,"E13.filletArc"),sQuery(id+"F0.wireOp",EDGE,"E14.filletArc"),sQuery(id+"F0.wireOp",EDGE,"E15.filletArc"),sQuery(id+"F0.wireOp",EDGE,"E16.filletArc"),subQ1,subQ2,subQ3,subQ4,subQ5,subQ0,sQuery(id+"F0.wireOp",EDGE,"E26"),sQuery(id+"F0.wireOp",EDGE,"E27"),sQuery(id+"F0.wireOp",EDGE,"E28"),sQuery(id+"F0.wireOp",EDGE,"E29"),sQuery(id+"F0.wireOp",EDGE,"E30"),sQuery(id+"F0.wireOp",EDGE,"E31"),sQuery(id+"F0.wireOp",EDGE,"E32"),sQuery(id+"F0.wireOp",EDGE,"E33"),sQuery(id+"F0.wireOp",EDGE,"E34"),sQuery(id+"F0.wireOp",EDGE,"E35"),sQuery(id+"F0.wireOp",EDGE,"E36"),sQuery(id+"F0.wireOp",EDGE,"E37")])],"isStart":false})});}
            var sketch = newSketch(context, id + "F7", { "sketchPlane" : qUnion([Q0])});
            skLineSegment(sketch, "E130.bottom", {"start": v(-237.07, -5.97) * mm, "end": v(-198.47, -5.97) * mm});
            skLineSegment(sketch, "E130.top", {"start": v(-237.07, -3.18) * mm, "end": v(-198.47, -3.18) * mm});
            skLineSegment(sketch, "E130.left", {"start": v(-237.07, -5.97) * mm, "end": v(-237.07, -3.18) * mm});
            skLineSegment(sketch, "E130.right", {"start": v(-198.47, -5.97) * mm, "end": v(-198.47, -3.18) * mm});
            skPoint(sketch, "E131", {"position": v(-217.77, -5.97) * mm});
            skSolve(sketch);
        }
        {
            var Q0;
            Q0=qSketchRegion(id+"F7",true);
            var Q1;
            {var subQ0=sQuery(id+"F0.wireOp",EDGE,"E37");var subQ1=sQuery(id+"F0.wireOp",EDGE,"E36");var subQ2=sQuery(id+"F0.wireOp",EDGE,"E35");var subQ3=sQuery(id+"F0.wireOp",EDGE,"E34");var subQ4=sQuery(id+"F0.wireOp",EDGE,"E33");var subQ5=sQuery(id+"F0.wireOp",EDGE,"E32");var subQ6=sQuery(id+"F0.wireOp",EDGE,"E31");var subQ7=sQuery(id+"F0.wireOp",EDGE,"E30");var subQ8=sQuery(id+"F0.wireOp",EDGE,"E29");var subQ9=sQuery(id+"F0.wireOp",EDGE,"E28");var subQ10=sQuery(id+"F0.wireOp",EDGE,"E27");var subQ11=sQuery(id+"F0.wireOp",EDGE,"E26");var subQ12=sQuery(id+"F0.wireOp",EDGE,"E25");var subQ13=sQuery(id+"F0.wireOp",EDGE,"E24");var subQ14=sQuery(id+"F0.wireOp",EDGE,"E23");var subQ15=sQuery(id+"F0.wireOp",EDGE,"E22");var subQ16=sQuery(id+"F0.wireOp",EDGE,"E21");var subQ17=sQuery(id+"F0.wireOp",EDGE,"E20");Q1=makeQuery(id+"F2.boolean.opBoolean","MERGE",FACE,{"derivedFrom":[makeQuery(id+"F1.opExtrude","CAP_FACE",FACE,{"disambiguationData":[OSD([sQuery(id+"F0.wireOp",EDGE,"E0.1"),sQuery(id+"F0.wireOp",EDGE,"E0.3"),sQuery(id+"F0.wireOp",EDGE,"E0.4"),sQuery(id+"F0.wireOp",EDGE,"E0.5"),sQuery(id+"F0.wireOp",EDGE,"E1.0"),sQuery(id+"F0.wireOp",EDGE,"E1.1"),sQuery(id+"F0.wireOp",EDGE,"E1.2"),sQuery(id+"F0.wireOp",EDGE,"E1.3"),sQuery(id+"F0.wireOp",EDGE,"E1.5"),sQuery(id+"F0.wireOp",EDGE,"E2.0"),sQuery(id+"F0.wireOp",EDGE,"E2.1"),sQuery(id+"F0.wireOp",EDGE,"E2.2"),sQuery(id+"F0.wireOp",EDGE,"E2.4"),sQuery(id+"F0.wireOp",EDGE,"E2.5"),sQuery(id+"F0.wireOp",EDGE,"E3.filletArc"),sQuery(id+"F0.wireOp",EDGE,"E4.filletArc"),sQuery(id+"F0.wireOp",EDGE,"E5.filletArc"),sQuery(id+"F0.wireOp",EDGE,"E6.filletArc"),sQuery(id+"F0.wireOp",EDGE,"E7.filletArc"),sQuery(id+"F0.wireOp",EDGE,"E8.filletArc"),sQuery(id+"F0.wireOp",EDGE,"E9.filletArc"),sQuery(id+"F0.wireOp",EDGE,"E10.filletArc"),sQuery(id+"F0.wireOp",EDGE,"E11.filletArc"),sQuery(id+"F0.wireOp",EDGE,"E12.filletArc"),sQuery(id+"F0.wireOp",EDGE,"E13.filletArc"),sQuery(id+"F0.wireOp",EDGE,"E14.filletArc"),sQuery(id+"F0.wireOp",EDGE,"E15.filletArc"),sQuery(id+"F0.wireOp",EDGE,"E16.filletArc"),subQ17,subQ16,subQ15,subQ14,subQ13,subQ12,subQ11,subQ10,subQ9,subQ8,subQ7,subQ6,subQ5,subQ4,subQ3,subQ2,subQ1,subQ0])],"isStart":true}),makeQuery(id+"F2.opExtrude","CAP_FACE",FACE,{"disambiguationData":[OSD([subQ17])],"isStart":true}),makeQuery(id+"F2.opExtrude","CAP_FACE",FACE,{"disambiguationData":[OSD([subQ16])],"isStart":true}),makeQuery(id+"F2.opExtrude","CAP_FACE",FACE,{"disambiguationData":[OSD([subQ15])],"isStart":true}),makeQuery(id+"F2.opExtrude","CAP_FACE",FACE,{"disambiguationData":[OSD([subQ14])],"isStart":true}),makeQuery(id+"F2.opExtrude","CAP_FACE",FACE,{"disambiguationData":[OSD([subQ13])],"isStart":true}),makeQuery(id+"F2.opExtrude","CAP_FACE",FACE,{"disambiguationData":[OSD([subQ12])],"isStart":true}),makeQuery(id+"F2.opExtrude","CAP_FACE",FACE,{"disambiguationData":[OSD([subQ11])],"isStart":true}),makeQuery(id+"F2.opExtrude","CAP_FACE",FACE,{"disambiguationData":[OSD([subQ10])],"isStart":true}),makeQuery(id+"F2.opExtrude","CAP_FACE",FACE,{"disambiguationData":[OSD([subQ9])],"isStart":true}),makeQuery(id+"F2.opExtrude","CAP_FACE",FACE,{"disambiguationData":[OSD([subQ8])],"isStart":true}),makeQuery(id+"F2.opExtrude","CAP_FACE",FACE,{"disambiguationData":[OSD([subQ7])],"isStart":true}),makeQuery(id+"F2.opExtrude","CAP_FACE",FACE,{"disambiguationData":[OSD([subQ6])],"isStart":true}),makeQuery(id+"F2.opExtrude","CAP_FACE",FACE,{"disambiguationData":[OSD([subQ5])],"isStart":true}),makeQuery(id+"F2.opExtrude","CAP_FACE",FACE,{"disambiguationData":[OSD([subQ4])],"isStart":true}),makeQuery(id+"F2.opExtrude","CAP_FACE",FACE,{"disambiguationData":[OSD([subQ3])],"isStart":true}),makeQuery(id+"F2.opExtrude","CAP_FACE",FACE,{"disambiguationData":[OSD([subQ2])],"isStart":true}),makeQuery(id+"F2.opExtrude","CAP_FACE",FACE,{"disambiguationData":[OSD([subQ1])],"isStart":true}),makeQuery(id+"F2.opExtrude","CAP_FACE",FACE,{"disambiguationData":[OSD([subQ0])],"isStart":true})]});}
            extrude(context, id + "F8", {"entities" : qUnion([Q0]), "operationType" : NewBodyOperationType.ADD, "endBound" : BoundingType.UP_TO_SURFACE, "oppositeDirection" : true, "endBoundEntityFace" : qUnion([Q1]), "depth" : 25.4 * mm});
        }
        {
            var Q0;
            Q0=makeQuery(id+"F1.opExtrude","SWEPT_FACE",FACE,{"disambiguationData":[OSD([sQuery(id+"F0.wireOp",EDGE,"E1.0")])]});
            var Q1;
            Q1=makeQuery(id+"F1.opExtrude","SWEPT_FACE",FACE,{"disambiguationData":[OSD([sQuery(id+"F0.wireOp",EDGE,"E1.3")])]});
            cPlane(context, id + "F9", {"entities" : qUnion([Q0, Q1]), "cplaneType" : CPlaneType.MID_PLANE, "offset" : 25.4 * mm, "width" : 152.4 * mm, "height" : 152.4 * mm});
        }
        {
            var Q0;
            Q0=makeQuery(id+"F1.opExtrude","SWEPT_FACE",FACE,{"disambiguationData":[OSD([sQuery(id+"F0.wireOp",EDGE,"E1.1")])]});
            var Q1;
            Q1=makeQuery(id+"F1.opExtrude","SWEPT_FACE",FACE,{"disambiguationData":[OSD([sQuery(id+"F0.wireOp",EDGE,"E0.5")])]});
            cPlane(context, id + "F10", {"entities" : qUnion([Q0, Q1]), "cplaneType" : CPlaneType.MID_PLANE, "offset" : 25.4 * mm, "width" : 152.4 * mm, "height" : 152.4 * mm});
        }
        {
            var Q0;
            Q0=qCreatedBy(id+"F9.planeOp",FACE);
            var sketch = newSketch(context, id + "F11", { "sketchPlane" : qUnion([Q0])});
            skLineSegment(sketch, "E132", {"start": v(-217.77, 12.59) * mm, "end": v(-217.77, 74.92) * mm, "construction": true});
            skSolve(sketch);
        }
        {
            var Q0;
            {var subQ0=sQuery(id+"F7.wireOp",EDGE,"E130.right");var subQ1=sQuery(id+"F7.wireOp",EDGE,"E130.left");var subQ2=sQuery(id+"F7.wireOp",EDGE,"E130.top");var subQ3=sQuery(id+"F7.wireOp",EDGE,"E130.bottom");var subQ4=sQuery(id+"F0.wireOp",EDGE,"E25");var subQ5=sQuery(id+"F0.wireOp",EDGE,"E20");var subQ6=sQuery(id+"F0.wireOp",EDGE,"E21");var subQ7=sQuery(id+"F0.wireOp",EDGE,"E22");var subQ8=sQuery(id+"F0.wireOp",EDGE,"E23");var subQ9=sQuery(id+"F0.wireOp",EDGE,"E24");var subQ10=sQuery(id+"F0.wireOp",EDGE,"E37");var subQ11=sQuery(id+"F0.wireOp",EDGE,"E36");var subQ12=sQuery(id+"F0.wireOp",EDGE,"E35");var subQ13=sQuery(id+"F0.wireOp",EDGE,"E34");var subQ14=sQuery(id+"F0.wireOp",EDGE,"E33");var subQ15=sQuery(id+"F0.wireOp",EDGE,"E32");var subQ16=sQuery(id+"F0.wireOp",EDGE,"E31");var subQ17=sQuery(id+"F0.wireOp",EDGE,"E30");var subQ18=sQuery(id+"F0.wireOp",EDGE,"E29");var subQ19=sQuery(id+"F0.wireOp",EDGE,"E28");var subQ20=sQuery(id+"F0.wireOp",EDGE,"E27");var subQ21=sQuery(id+"F0.wireOp",EDGE,"E26");var subQ22=sQuery(id+"F0.wireOp",EDGE,"E16.filletArc");var subQ23=sQuery(id+"F0.wireOp",EDGE,"E15.filletArc");var subQ24=sQuery(id+"F0.wireOp",EDGE,"E14.filletArc");var subQ25=sQuery(id+"F0.wireOp",EDGE,"E13.filletArc");var subQ26=sQuery(id+"F0.wireOp",EDGE,"E12.filletArc");var subQ27=sQuery(id+"F0.wireOp",EDGE,"E11.filletArc");var subQ28=sQuery(id+"F0.wireOp",EDGE,"E10.filletArc");var subQ29=sQuery(id+"F0.wireOp",EDGE,"E9.filletArc");var subQ30=sQuery(id+"F0.wireOp",EDGE,"E8.filletArc");var subQ31=sQuery(id+"F0.wireOp",EDGE,"E7.filletArc");var subQ32=sQuery(id+"F0.wireOp",EDGE,"E6.filletArc");var subQ33=sQuery(id+"F0.wireOp",EDGE,"E5.filletArc");var subQ34=sQuery(id+"F0.wireOp",EDGE,"E4.filletArc");var subQ35=sQuery(id+"F0.wireOp",EDGE,"E3.filletArc");var subQ36=sQuery(id+"F0.wireOp",EDGE,"E2.5");var subQ37=sQuery(id+"F0.wireOp",EDGE,"E2.4");var subQ38=sQuery(id+"F0.wireOp",EDGE,"E2.2");var subQ39=sQuery(id+"F0.wireOp",EDGE,"E2.1");var subQ40=sQuery(id+"F0.wireOp",EDGE,"E2.0");var subQ41=sQuery(id+"F0.wireOp",EDGE,"E1.5");var subQ42=sQuery(id+"F0.wireOp",EDGE,"E1.3");var subQ43=sQuery(id+"F0.wireOp",EDGE,"E1.2");var subQ44=sQuery(id+"F0.wireOp",EDGE,"E1.1");var subQ45=sQuery(id+"F0.wireOp",EDGE,"E1.0");var subQ46=sQuery(id+"F0.wireOp",EDGE,"E0.5");var subQ47=sQuery(id+"F0.wireOp",EDGE,"E0.4");var subQ48=sQuery(id+"F0.wireOp",EDGE,"E0.3");var subQ49=sQuery(id+"F0.wireOp",EDGE,"E0.1");var subQ50=makeQuery(id+"F1.opExtrude","CAP_FACE",FACE,{"disambiguationData":[OSD([subQ49,subQ48,subQ47,subQ46,subQ45,subQ44,subQ43,subQ42,subQ41,subQ40,subQ39,subQ38,subQ37,subQ36,subQ35,subQ34,subQ33,subQ32,subQ31,subQ30,subQ29,subQ28,subQ27,subQ26,subQ25,subQ24,subQ23,subQ22,subQ5,subQ6,subQ7,subQ8,subQ9,subQ4,subQ21,subQ20,subQ19,subQ18,subQ17,subQ16,subQ15,subQ14,subQ13,subQ12,subQ11,subQ10])],"isStart":false});Q0=makeQuery(id+"FArHMtP67R58qOK_1.1.FbB5umPfR1j8SLP_1.5.F8.boolean.opBoolean","MERGE",FACE,{"derivedFrom":[makeQuery(id+"FArHMtP67R58qOK_1.1.FbB5umPfR1j8SLP_1.4.F8.boolean.opBoolean","MERGE",FACE,{"derivedFrom":[makeQuery(id+"FArHMtP67R58qOK_1.1.FbB5umPfR1j8SLP_1.3.F8.boolean.opBoolean","MERGE",FACE,{"derivedFrom":[makeQuery(id+"FArHMtP67R58qOK_1.1.FbB5umPfR1j8SLP_1.2.F8.boolean.opBoolean","MERGE",FACE,{"derivedFrom":[makeQuery(id+"FArHMtP67R58qOK_1.1.FbB5umPfR1j8SLP_1.1.F8.boolean.opBoolean","MERGE",FACE,{"derivedFrom":[makeQuery(id+"FArHMtP67R58qOK_1.1.F8.boolean.opBoolean","MERGE",FACE,{"derivedFrom":[makeQuery(id+"F0aKffUkCtTZm95_1.boolean.opBoolean","SPLIT",FACE,{"disambiguationData":[TD([makeQuery(id+"F1.opExtrude","SWEPT_FACE",FACE,{"disambiguationData":[OSD([subQ21])]})])],"derivedFrom":subQ50}),makeQuery(id+"FZtU8A5xYbT4ezZ_1.1.FbB5umPfR1j8SLP_1.5.F8.boolean.opBoolean","MERGE",FACE,{"derivedFrom":[makeQuery(id+"FZtU8A5xYbT4ezZ_1.1.FbB5umPfR1j8SLP_1.4.F8.boolean.opBoolean","MERGE",FACE,{"derivedFrom":[makeQuery(id+"FZtU8A5xYbT4ezZ_1.1.FbB5umPfR1j8SLP_1.3.F8.boolean.opBoolean","MERGE",FACE,{"derivedFrom":[makeQuery(id+"FZtU8A5xYbT4ezZ_1.1.FbB5umPfR1j8SLP_1.2.F8.boolean.opBoolean","MERGE",FACE,{"derivedFrom":[makeQuery(id+"FZtU8A5xYbT4ezZ_1.1.FbB5umPfR1j8SLP_1.1.F8.boolean.opBoolean","MERGE",FACE,{"derivedFrom":[makeQuery(id+"FZtU8A5xYbT4ezZ_1.1.F8.boolean.opBoolean","MERGE",FACE,{"derivedFrom":[makeQuery(id+"F0aKffUkCtTZm95_1.boolean.opBoolean","SPLIT",FACE,{"disambiguationData":[TD([makeQuery(id+"F1.opExtrude","SWEPT_FACE",FACE,{"disambiguationData":[OSD([subQ15])]})])],"derivedFrom":subQ50}),makeQuery(id+"FbB5umPfR1j8SLP_1.5.F8.boolean.opBoolean","MERGE",FACE,{"derivedFrom":[makeQuery(id+"FbB5umPfR1j8SLP_1.4.F8.boolean.opBoolean","MERGE",FACE,{"derivedFrom":[makeQuery(id+"FbB5umPfR1j8SLP_1.3.F8.boolean.opBoolean","MERGE",FACE,{"derivedFrom":[makeQuery(id+"FbB5umPfR1j8SLP_1.2.F8.boolean.opBoolean","MERGE",FACE,{"derivedFrom":[makeQuery(id+"FbB5umPfR1j8SLP_1.1.F8.boolean.opBoolean","MERGE",FACE,{"derivedFrom":[makeQuery(id+"F8.boolean.opBoolean","MERGE",FACE,{"derivedFrom":[makeQuery(id+"F0aKffUkCtTZm95_1.boolean.opBoolean","SPLIT",FACE,{"disambiguationData":[TD([makeQuery(id+"F1.opExtrude","SWEPT_FACE",FACE,{"disambiguationData":[OSD([subQ49])]})])],"derivedFrom":subQ50}),makeQuery(id+"F0aKffUkCtTZm95_1.boolean.opBoolean","SPLIT",FACE,{"disambiguationData":[TD([makeQuery(id+"F1.opExtrude","SWEPT_FACE",FACE,{"disambiguationData":[OSD([subQ5])]})])],"derivedFrom":subQ50}),makeQuery(id+"F8.opExtrude","CAP_FACE",FACE,{"disambiguationData":[OSD([subQ3,subQ2,subQ1,subQ0])],"isStart":true})]}),makeQuery(id+"FbB5umPfR1j8SLP_1.1.F8.opExtrude","CAP_FACE",FACE,{"disambiguationData":[OSD([subQ3,subQ2,subQ1,subQ0])],"isStart":true})]}),makeQuery(id+"FbB5umPfR1j8SLP_1.2.F8.opExtrude","CAP_FACE",FACE,{"disambiguationData":[OSD([subQ3,subQ2,subQ1,subQ0])],"isStart":true})]}),makeQuery(id+"FbB5umPfR1j8SLP_1.3.F8.opExtrude","CAP_FACE",FACE,{"disambiguationData":[OSD([subQ3,subQ2,subQ1,subQ0])],"isStart":true})]}),makeQuery(id+"FbB5umPfR1j8SLP_1.4.F8.opExtrude","CAP_FACE",FACE,{"disambiguationData":[OSD([subQ3,subQ2,subQ1,subQ0])],"isStart":true})]}),makeQuery(id+"FbB5umPfR1j8SLP_1.5.F8.opExtrude","CAP_FACE",FACE,{"disambiguationData":[OSD([subQ3,subQ2,subQ1,subQ0])],"isStart":true})]}),makeQuery(id+"FZtU8A5xYbT4ezZ_1.1.F8.opExtrude","CAP_FACE",FACE,{"disambiguationData":[OSD([subQ3,subQ2,subQ1,subQ0])],"isStart":true})]}),makeQuery(id+"FZtU8A5xYbT4ezZ_1.1.FbB5umPfR1j8SLP_1.1.F8.opExtrude","CAP_FACE",FACE,{"disambiguationData":[OSD([subQ3,subQ2,subQ1,subQ0])],"isStart":true})]}),makeQuery(id+"FZtU8A5xYbT4ezZ_1.1.FbB5umPfR1j8SLP_1.2.F8.opExtrude","CAP_FACE",FACE,{"disambiguationData":[OSD([subQ3,subQ2,subQ1,subQ0])],"isStart":true})]}),makeQuery(id+"FZtU8A5xYbT4ezZ_1.1.FbB5umPfR1j8SLP_1.3.F8.opExtrude","CAP_FACE",FACE,{"disambiguationData":[OSD([subQ3,subQ2,subQ1,subQ0])],"isStart":true})]}),makeQuery(id+"FZtU8A5xYbT4ezZ_1.1.FbB5umPfR1j8SLP_1.4.F8.opExtrude","CAP_FACE",FACE,{"disambiguationData":[OSD([subQ3,subQ2,subQ1,subQ0])],"isStart":true})]}),makeQuery(id+"FZtU8A5xYbT4ezZ_1.1.FbB5umPfR1j8SLP_1.5.F8.opExtrude","CAP_FACE",FACE,{"disambiguationData":[OSD([subQ3,subQ2,subQ1,subQ0])],"isStart":true})]}),makeQuery(id+"FArHMtP67R58qOK_1.1.F8.opExtrude","CAP_FACE",FACE,{"disambiguationData":[OSD([subQ3,subQ2,subQ1,subQ0])],"isStart":true})]}),makeQuery(id+"FArHMtP67R58qOK_1.1.FbB5umPfR1j8SLP_1.1.F8.opExtrude","CAP_FACE",FACE,{"disambiguationData":[OSD([subQ3,subQ2,subQ1,subQ0])],"isStart":true})]}),makeQuery(id+"FArHMtP67R58qOK_1.1.FbB5umPfR1j8SLP_1.2.F8.opExtrude","CAP_FACE",FACE,{"disambiguationData":[OSD([subQ3,subQ2,subQ1,subQ0])],"isStart":true})]}),makeQuery(id+"FArHMtP67R58qOK_1.1.FbB5umPfR1j8SLP_1.3.F8.opExtrude","CAP_FACE",FACE,{"disambiguationData":[OSD([subQ3,subQ2,subQ1,subQ0])],"isStart":true})]}),makeQuery(id+"FArHMtP67R58qOK_1.1.FbB5umPfR1j8SLP_1.4.F8.opExtrude","CAP_FACE",FACE,{"disambiguationData":[OSD([subQ3,subQ2,subQ1,subQ0])],"isStart":true})]}),makeQuery(id+"FArHMtP67R58qOK_1.1.FbB5umPfR1j8SLP_1.5.F8.opExtrude","CAP_FACE",FACE,{"disambiguationData":[OSD([subQ3,subQ2,subQ1,subQ0])],"isStart":true})]});}
            var sketch = newSketch(context, id + "F12", { "sketchPlane" : qUnion([Q0])});
            skLineSegment(sketch, "E133.bottom", {"start": v(-3.73, -87.63) * mm, "end": v(57.74, -87.63) * mm, "construction": true});
            skLineSegment(sketch, "E133.top", {"start": v(-3.73, -3.3) * mm, "end": v(57.74, -3.3) * mm, "construction": true});
            skLineSegment(sketch, "E133.left", {"start": v(-3.73, -87.63) * mm, "end": v(-3.73, -3.3) * mm, "construction": true});
            skLineSegment(sketch, "E133.right", {"start": v(57.74, -87.63) * mm, "end": v(57.74, -3.3) * mm, "construction": true});
            skLineSegment(sketch, "E134.bottom", {"start": v(-53, -3.3) * mm, "end": v(-16.43, -3.3) * mm, "construction": true});
            skLineSegment(sketch, "E134.top", {"start": v(-53, -41.4) * mm, "end": v(-16.43, -41.4) * mm, "construction": true});
            skLineSegment(sketch, "E134.left", {"start": v(-53, -3.3) * mm, "end": v(-53, -41.4) * mm, "construction": true});
            skLineSegment(sketch, "E134.right", {"start": v(-16.43, -3.3) * mm, "end": v(-16.43, -41.4) * mm, "construction": true});
            skCircle(sketch, "E135", {"center": v(-53, -3.3) * mm, "radius": 1.14 * mm});
            skCircle(sketch, "E136", {"center": v(-16.43, -3.3) * mm, "radius": 1.14 * mm});
            skCircle(sketch, "E137", {"center": v(-53, -41.4) * mm, "radius": 1.14 * mm});
            skCircle(sketch, "E138", {"center": v(-3.73, -87.63) * mm, "radius": 1.14 * mm});
            skCircle(sketch, "E139", {"center": v(57.74, -87.63) * mm, "radius": 1.14 * mm});
            skCircle(sketch, "E140", {"center": v(57.74, -3.3) * mm, "radius": 1.14 * mm});
            skCircle(sketch, "E141", {"center": v(-3.73, -3.3) * mm, "radius": 1.14 * mm});
            skCircle(sketch, "E142", {"center": v(-16.43, -41.4) * mm, "radius": 1.14 * mm});
            skSolve(sketch);
        }
        {
            var Q0;
            Q0=qSketchRegion(id+"F12",true);
            var Q1;
            {var subQ0=sQuery(id+"F0.wireOp",EDGE,"E37");var subQ1=sQuery(id+"F0.wireOp",EDGE,"E36");var subQ2=sQuery(id+"F0.wireOp",EDGE,"E35");var subQ3=sQuery(id+"F0.wireOp",EDGE,"E34");var subQ4=sQuery(id+"F0.wireOp",EDGE,"E33");var subQ5=sQuery(id+"F0.wireOp",EDGE,"E32");var subQ6=sQuery(id+"F0.wireOp",EDGE,"E31");var subQ7=sQuery(id+"F0.wireOp",EDGE,"E30");var subQ8=sQuery(id+"F0.wireOp",EDGE,"E29");var subQ9=sQuery(id+"F0.wireOp",EDGE,"E28");var subQ10=sQuery(id+"F0.wireOp",EDGE,"E27");var subQ11=sQuery(id+"F0.wireOp",EDGE,"E26");var subQ12=sQuery(id+"F0.wireOp",EDGE,"E25");var subQ13=sQuery(id+"F0.wireOp",EDGE,"E24");var subQ14=sQuery(id+"F0.wireOp",EDGE,"E23");var subQ15=sQuery(id+"F0.wireOp",EDGE,"E22");var subQ16=sQuery(id+"F0.wireOp",EDGE,"E21");var subQ17=sQuery(id+"F0.wireOp",EDGE,"E20");var subQ18=sQuery(id+"F0.wireOp",EDGE,"E16.filletArc");var subQ19=sQuery(id+"F0.wireOp",EDGE,"E15.filletArc");var subQ20=sQuery(id+"F0.wireOp",EDGE,"E14.filletArc");var subQ21=sQuery(id+"F0.wireOp",EDGE,"E13.filletArc");var subQ22=sQuery(id+"F0.wireOp",EDGE,"E12.filletArc");var subQ23=sQuery(id+"F0.wireOp",EDGE,"E11.filletArc");var subQ24=sQuery(id+"F0.wireOp",EDGE,"E10.filletArc");var subQ25=sQuery(id+"F0.wireOp",EDGE,"E9.filletArc");var subQ26=sQuery(id+"F0.wireOp",EDGE,"E8.filletArc");var subQ27=sQuery(id+"F0.wireOp",EDGE,"E7.filletArc");var subQ28=sQuery(id+"F0.wireOp",EDGE,"E6.filletArc");var subQ29=sQuery(id+"F0.wireOp",EDGE,"E5.filletArc");var subQ30=sQuery(id+"F0.wireOp",EDGE,"E4.filletArc");var subQ31=sQuery(id+"F0.wireOp",EDGE,"E3.filletArc");var subQ32=sQuery(id+"F0.wireOp",EDGE,"E2.5");var subQ33=sQuery(id+"F0.wireOp",EDGE,"E2.4");var subQ34=sQuery(id+"F0.wireOp",EDGE,"E2.2");var subQ35=sQuery(id+"F0.wireOp",EDGE,"E2.1");var subQ36=sQuery(id+"F0.wireOp",EDGE,"E2.0");var subQ37=sQuery(id+"F0.wireOp",EDGE,"E1.5");var subQ38=sQuery(id+"F0.wireOp",EDGE,"E1.3");var subQ39=sQuery(id+"F0.wireOp",EDGE,"E1.2");var subQ40=sQuery(id+"F0.wireOp",EDGE,"E1.1");var subQ41=sQuery(id+"F0.wireOp",EDGE,"E1.0");var subQ42=sQuery(id+"F0.wireOp",EDGE,"E0.5");var subQ43=sQuery(id+"F0.wireOp",EDGE,"E0.4");var subQ44=sQuery(id+"F0.wireOp",EDGE,"E0.3");var subQ45=sQuery(id+"F0.wireOp",EDGE,"E0.1");Q1=makeQuery(id+"FArHMtP67R58qOK_1.1.FbB5umPfR1j8SLP_1.5.F8.boolean.opBoolean","MERGE",FACE,{"derivedFrom":[makeQuery(id+"FArHMtP67R58qOK_1.1.FbB5umPfR1j8SLP_1.4.F8.boolean.opBoolean","MERGE",FACE,{"derivedFrom":[makeQuery(id+"FArHMtP67R58qOK_1.1.FbB5umPfR1j8SLP_1.3.F8.boolean.opBoolean","MERGE",FACE,{"derivedFrom":[makeQuery(id+"FArHMtP67R58qOK_1.1.FbB5umPfR1j8SLP_1.2.F8.boolean.opBoolean","MERGE",FACE,{"derivedFrom":[makeQuery(id+"FArHMtP67R58qOK_1.1.FbB5umPfR1j8SLP_1.1.F8.boolean.opBoolean","MERGE",FACE,{"derivedFrom":[makeQuery(id+"FArHMtP67R58qOK_1.1.F8.boolean.opBoolean","MERGE",FACE,{"derivedFrom":[makeQuery(id+"FZtU8A5xYbT4ezZ_1.1.FbB5umPfR1j8SLP_1.5.F8.boolean.opBoolean","MERGE",FACE,{"derivedFrom":[makeQuery(id+"FZtU8A5xYbT4ezZ_1.1.FbB5umPfR1j8SLP_1.4.F8.boolean.opBoolean","MERGE",FACE,{"derivedFrom":[makeQuery(id+"FZtU8A5xYbT4ezZ_1.1.FbB5umPfR1j8SLP_1.3.F8.boolean.opBoolean","MERGE",FACE,{"derivedFrom":[makeQuery(id+"FZtU8A5xYbT4ezZ_1.1.FbB5umPfR1j8SLP_1.2.F8.boolean.opBoolean","MERGE",FACE,{"derivedFrom":[makeQuery(id+"FZtU8A5xYbT4ezZ_1.1.FbB5umPfR1j8SLP_1.1.F8.boolean.opBoolean","MERGE",FACE,{"derivedFrom":[makeQuery(id+"FZtU8A5xYbT4ezZ_1.1.F8.boolean.opBoolean","MERGE",FACE,{"derivedFrom":[makeQuery(id+"FbB5umPfR1j8SLP_1.5.F8.boolean.opBoolean","MERGE",FACE,{"derivedFrom":[makeQuery(id+"FbB5umPfR1j8SLP_1.4.F8.boolean.opBoolean","MERGE",FACE,{"derivedFrom":[makeQuery(id+"FbB5umPfR1j8SLP_1.3.F8.boolean.opBoolean","MERGE",FACE,{"derivedFrom":[makeQuery(id+"FbB5umPfR1j8SLP_1.2.F8.boolean.opBoolean","MERGE",FACE,{"derivedFrom":[makeQuery(id+"FbB5umPfR1j8SLP_1.1.F8.boolean.opBoolean","MERGE",FACE,{"derivedFrom":[makeQuery(id+"F8.boolean.opBoolean","MERGE",FACE,{"derivedFrom":[makeQuery(id+"F2.boolean.opBoolean","MERGE",FACE,{"derivedFrom":[makeQuery(id+"F1.opExtrude","CAP_FACE",FACE,{"disambiguationData":[OSD([subQ45,subQ44,subQ43,subQ42,subQ41,subQ40,subQ39,subQ38,subQ37,subQ36,subQ35,subQ34,subQ33,subQ32,subQ31,subQ30,subQ29,subQ28,subQ27,subQ26,subQ25,subQ24,subQ23,subQ22,subQ21,subQ20,subQ19,subQ18,subQ17,subQ16,subQ15,subQ14,subQ13,subQ12,subQ11,subQ10,subQ9,subQ8,subQ7,subQ6,subQ5,subQ4,subQ3,subQ2,subQ1,subQ0])],"isStart":true}),makeQuery(id+"F2.opExtrude","CAP_FACE",FACE,{"disambiguationData":[OSD([subQ17])],"isStart":true}),makeQuery(id+"F2.opExtrude","CAP_FACE",FACE,{"disambiguationData":[OSD([subQ16])],"isStart":true}),makeQuery(id+"F2.opExtrude","CAP_FACE",FACE,{"disambiguationData":[OSD([subQ15])],"isStart":true}),makeQuery(id+"F2.opExtrude","CAP_FACE",FACE,{"disambiguationData":[OSD([subQ14])],"isStart":true}),makeQuery(id+"F2.opExtrude","CAP_FACE",FACE,{"disambiguationData":[OSD([subQ13])],"isStart":true}),makeQuery(id+"F2.opExtrude","CAP_FACE",FACE,{"disambiguationData":[OSD([subQ12])],"isStart":true}),makeQuery(id+"F2.opExtrude","CAP_FACE",FACE,{"disambiguationData":[OSD([subQ11])],"isStart":true}),makeQuery(id+"F2.opExtrude","CAP_FACE",FACE,{"disambiguationData":[OSD([subQ10])],"isStart":true}),makeQuery(id+"F2.opExtrude","CAP_FACE",FACE,{"disambiguationData":[OSD([subQ9])],"isStart":true}),makeQuery(id+"F2.opExtrude","CAP_FACE",FACE,{"disambiguationData":[OSD([subQ8])],"isStart":true}),makeQuery(id+"F2.opExtrude","CAP_FACE",FACE,{"disambiguationData":[OSD([subQ7])],"isStart":true}),makeQuery(id+"F2.opExtrude","CAP_FACE",FACE,{"disambiguationData":[OSD([subQ6])],"isStart":true}),makeQuery(id+"F2.opExtrude","CAP_FACE",FACE,{"disambiguationData":[OSD([subQ5])],"isStart":true}),makeQuery(id+"F2.opExtrude","CAP_FACE",FACE,{"disambiguationData":[OSD([subQ4])],"isStart":true}),makeQuery(id+"F2.opExtrude","CAP_FACE",FACE,{"disambiguationData":[OSD([subQ3])],"isStart":true}),makeQuery(id+"F2.opExtrude","CAP_FACE",FACE,{"disambiguationData":[OSD([subQ2])],"isStart":true}),makeQuery(id+"F2.opExtrude","CAP_FACE",FACE,{"disambiguationData":[OSD([subQ1])],"isStart":true}),makeQuery(id+"F2.opExtrude","CAP_FACE",FACE,{"disambiguationData":[OSD([subQ0])],"isStart":true})]}),makeQuery(id+"F8.opExtrude","CAP_FACE",FACE,{"disambiguationData":[OSD([subQ45,subQ44,subQ43,subQ42,subQ41,subQ40,subQ39,subQ38,subQ37,subQ36,subQ35,subQ34,subQ33,subQ32,subQ31,subQ30,subQ29,subQ28,subQ27,subQ26,subQ25,subQ24,subQ23,subQ22,subQ21,subQ20,subQ19,subQ18,subQ17,subQ16,subQ15,subQ14,subQ13,subQ12,subQ11,subQ10,subQ9,subQ8,subQ7,subQ6,subQ5,subQ4,subQ3,subQ2,subQ1,subQ0])],"isStart":false})]}),makeQuery(id+"FbB5umPfR1j8SLP_1.1.F8.opExtrude","CAP_FACE",FACE,{"disambiguationData":[OSD([subQ45,subQ44,subQ43,subQ42,subQ41,subQ40,subQ39,subQ38,subQ37,subQ36,subQ35,subQ34,subQ33,subQ32,subQ31,subQ30,subQ29,subQ28,subQ27,subQ26,subQ25,subQ24,subQ23,subQ22,subQ21,subQ20,subQ19,subQ18,subQ17,subQ16,subQ15,subQ14,subQ13,subQ12,subQ11,subQ10,subQ9,subQ8,subQ7,subQ6,subQ5,subQ4,subQ3,subQ2,subQ1,subQ0])],"isStart":false})]}),makeQuery(id+"FbB5umPfR1j8SLP_1.2.F8.opExtrude","CAP_FACE",FACE,{"disambiguationData":[OSD([subQ45,subQ44,subQ43,subQ42,subQ41,subQ40,subQ39,subQ38,subQ37,subQ36,subQ35,subQ34,subQ33,subQ32,subQ31,subQ30,subQ29,subQ28,subQ27,subQ26,subQ25,subQ24,subQ23,subQ22,subQ21,subQ20,subQ19,subQ18,subQ17,subQ16,subQ15,subQ14,subQ13,subQ12,subQ11,subQ10,subQ9,subQ8,subQ7,subQ6,subQ5,subQ4,subQ3,subQ2,subQ1,subQ0])],"isStart":false})]}),makeQuery(id+"FbB5umPfR1j8SLP_1.3.F8.opExtrude","CAP_FACE",FACE,{"disambiguationData":[OSD([subQ45,subQ44,subQ43,subQ42,subQ41,subQ40,subQ39,subQ38,subQ37,subQ36,subQ35,subQ34,subQ33,subQ32,subQ31,subQ30,subQ29,subQ28,subQ27,subQ26,subQ25,subQ24,subQ23,subQ22,subQ21,subQ20,subQ19,subQ18,subQ17,subQ16,subQ15,subQ14,subQ13,subQ12,subQ11,subQ10,subQ9,subQ8,subQ7,subQ6,subQ5,subQ4,subQ3,subQ2,subQ1,subQ0])],"isStart":false})]}),makeQuery(id+"FbB5umPfR1j8SLP_1.4.F8.opExtrude","CAP_FACE",FACE,{"disambiguationData":[OSD([subQ45,subQ44,subQ43,subQ42,subQ41,subQ40,subQ39,subQ38,subQ37,subQ36,subQ35,subQ34,subQ33,subQ32,subQ31,subQ30,subQ29,subQ28,subQ27,subQ26,subQ25,subQ24,subQ23,subQ22,subQ21,subQ20,subQ19,subQ18,subQ17,subQ16,subQ15,subQ14,subQ13,subQ12,subQ11,subQ10,subQ9,subQ8,subQ7,subQ6,subQ5,subQ4,subQ3,subQ2,subQ1,subQ0])],"isStart":false})]}),makeQuery(id+"FbB5umPfR1j8SLP_1.5.F8.opExtrude","CAP_FACE",FACE,{"disambiguationData":[OSD([subQ45,subQ44,subQ43,subQ42,subQ41,subQ40,subQ39,subQ38,subQ37,subQ36,subQ35,subQ34,subQ33,subQ32,subQ31,subQ30,subQ29,subQ28,subQ27,subQ26,subQ25,subQ24,subQ23,subQ22,subQ21,subQ20,subQ19,subQ18,subQ17,subQ16,subQ15,subQ14,subQ13,subQ12,subQ11,subQ10,subQ9,subQ8,subQ7,subQ6,subQ5,subQ4,subQ3,subQ2,subQ1,subQ0])],"isStart":false})]}),makeQuery(id+"FZtU8A5xYbT4ezZ_1.1.F8.opExtrude","CAP_FACE",FACE,{"disambiguationData":[OSD([subQ45,subQ44,subQ43,subQ42,subQ41,subQ40,subQ39,subQ38,subQ37,subQ36,subQ35,subQ34,subQ33,subQ32,subQ31,subQ30,subQ29,subQ28,subQ27,subQ26,subQ25,subQ24,subQ23,subQ22,subQ21,subQ20,subQ19,subQ18,subQ17,subQ16,subQ15,subQ14,subQ13,subQ12,subQ11,subQ10,subQ9,subQ8,subQ7,subQ6,subQ5,subQ4,subQ3,subQ2,subQ1,subQ0])],"isStart":false})]}),makeQuery(id+"FZtU8A5xYbT4ezZ_1.1.FbB5umPfR1j8SLP_1.1.F8.opExtrude","CAP_FACE",FACE,{"disambiguationData":[OSD([subQ45,subQ44,subQ43,subQ42,subQ41,subQ40,subQ39,subQ38,subQ37,subQ36,subQ35,subQ34,subQ33,subQ32,subQ31,subQ30,subQ29,subQ28,subQ27,subQ26,subQ25,subQ24,subQ23,subQ22,subQ21,subQ20,subQ19,subQ18,subQ17,subQ16,subQ15,subQ14,subQ13,subQ12,subQ11,subQ10,subQ9,subQ8,subQ7,subQ6,subQ5,subQ4,subQ3,subQ2,subQ1,subQ0])],"isStart":false})]}),makeQuery(id+"FZtU8A5xYbT4ezZ_1.1.FbB5umPfR1j8SLP_1.2.F8.opExtrude","CAP_FACE",FACE,{"disambiguationData":[OSD([subQ45,subQ44,subQ43,subQ42,subQ41,subQ40,subQ39,subQ38,subQ37,subQ36,subQ35,subQ34,subQ33,subQ32,subQ31,subQ30,subQ29,subQ28,subQ27,subQ26,subQ25,subQ24,subQ23,subQ22,subQ21,subQ20,subQ19,subQ18,subQ17,subQ16,subQ15,subQ14,subQ13,subQ12,subQ11,subQ10,subQ9,subQ8,subQ7,subQ6,subQ5,subQ4,subQ3,subQ2,subQ1,subQ0])],"isStart":false})]}),makeQuery(id+"FZtU8A5xYbT4ezZ_1.1.FbB5umPfR1j8SLP_1.3.F8.opExtrude","CAP_FACE",FACE,{"disambiguationData":[OSD([subQ45,subQ44,subQ43,subQ42,subQ41,subQ40,subQ39,subQ38,subQ37,subQ36,subQ35,subQ34,subQ33,subQ32,subQ31,subQ30,subQ29,subQ28,subQ27,subQ26,subQ25,subQ24,subQ23,subQ22,subQ21,subQ20,subQ19,subQ18,subQ17,subQ16,subQ15,subQ14,subQ13,subQ12,subQ11,subQ10,subQ9,subQ8,subQ7,subQ6,subQ5,subQ4,subQ3,subQ2,subQ1,subQ0])],"isStart":false})]}),makeQuery(id+"FZtU8A5xYbT4ezZ_1.1.FbB5umPfR1j8SLP_1.4.F8.opExtrude","CAP_FACE",FACE,{"disambiguationData":[OSD([subQ45,subQ44,subQ43,subQ42,subQ41,subQ40,subQ39,subQ38,subQ37,subQ36,subQ35,subQ34,subQ33,subQ32,subQ31,subQ30,subQ29,subQ28,subQ27,subQ26,subQ25,subQ24,subQ23,subQ22,subQ21,subQ20,subQ19,subQ18,subQ17,subQ16,subQ15,subQ14,subQ13,subQ12,subQ11,subQ10,subQ9,subQ8,subQ7,subQ6,subQ5,subQ4,subQ3,subQ2,subQ1,subQ0])],"isStart":false})]}),makeQuery(id+"FZtU8A5xYbT4ezZ_1.1.FbB5umPfR1j8SLP_1.5.F8.opExtrude","CAP_FACE",FACE,{"disambiguationData":[OSD([subQ45,subQ44,subQ43,subQ42,subQ41,subQ40,subQ39,subQ38,subQ37,subQ36,subQ35,subQ34,subQ33,subQ32,subQ31,subQ30,subQ29,subQ28,subQ27,subQ26,subQ25,subQ24,subQ23,subQ22,subQ21,subQ20,subQ19,subQ18,subQ17,subQ16,subQ15,subQ14,subQ13,subQ12,subQ11,subQ10,subQ9,subQ8,subQ7,subQ6,subQ5,subQ4,subQ3,subQ2,subQ1,subQ0])],"isStart":false})]}),makeQuery(id+"FArHMtP67R58qOK_1.1.F8.opExtrude","CAP_FACE",FACE,{"disambiguationData":[OSD([subQ45,subQ44,subQ43,subQ42,subQ41,subQ40,subQ39,subQ38,subQ37,subQ36,subQ35,subQ34,subQ33,subQ32,subQ31,subQ30,subQ29,subQ28,subQ27,subQ26,subQ25,subQ24,subQ23,subQ22,subQ21,subQ20,subQ19,subQ18,subQ17,subQ16,subQ15,subQ14,subQ13,subQ12,subQ11,subQ10,subQ9,subQ8,subQ7,subQ6,subQ5,subQ4,subQ3,subQ2,subQ1,subQ0])],"isStart":false})]}),makeQuery(id+"FArHMtP67R58qOK_1.1.FbB5umPfR1j8SLP_1.1.F8.opExtrude","CAP_FACE",FACE,{"disambiguationData":[OSD([subQ45,subQ44,subQ43,subQ42,subQ41,subQ40,subQ39,subQ38,subQ37,subQ36,subQ35,subQ34,subQ33,subQ32,subQ31,subQ30,subQ29,subQ28,subQ27,subQ26,subQ25,subQ24,subQ23,subQ22,subQ21,subQ20,subQ19,subQ18,subQ17,subQ16,subQ15,subQ14,subQ13,subQ12,subQ11,subQ10,subQ9,subQ8,subQ7,subQ6,subQ5,subQ4,subQ3,subQ2,subQ1,subQ0])],"isStart":false})]}),makeQuery(id+"FArHMtP67R58qOK_1.1.FbB5umPfR1j8SLP_1.2.F8.opExtrude","CAP_FACE",FACE,{"disambiguationData":[OSD([subQ45,subQ44,subQ43,subQ42,subQ41,subQ40,subQ39,subQ38,subQ37,subQ36,subQ35,subQ34,subQ33,subQ32,subQ31,subQ30,subQ29,subQ28,subQ27,subQ26,subQ25,subQ24,subQ23,subQ22,subQ21,subQ20,subQ19,subQ18,subQ17,subQ16,subQ15,subQ14,subQ13,subQ12,subQ11,subQ10,subQ9,subQ8,subQ7,subQ6,subQ5,subQ4,subQ3,subQ2,subQ1,subQ0])],"isStart":false})]}),makeQuery(id+"FArHMtP67R58qOK_1.1.FbB5umPfR1j8SLP_1.3.F8.opExtrude","CAP_FACE",FACE,{"disambiguationData":[OSD([subQ45,subQ44,subQ43,subQ42,subQ41,subQ40,subQ39,subQ38,subQ37,subQ36,subQ35,subQ34,subQ33,subQ32,subQ31,subQ30,subQ29,subQ28,subQ27,subQ26,subQ25,subQ24,subQ23,subQ22,subQ21,subQ20,subQ19,subQ18,subQ17,subQ16,subQ15,subQ14,subQ13,subQ12,subQ11,subQ10,subQ9,subQ8,subQ7,subQ6,subQ5,subQ4,subQ3,subQ2,subQ1,subQ0])],"isStart":false})]}),makeQuery(id+"FArHMtP67R58qOK_1.1.FbB5umPfR1j8SLP_1.4.F8.opExtrude","CAP_FACE",FACE,{"disambiguationData":[OSD([subQ45,subQ44,subQ43,subQ42,subQ41,subQ40,subQ39,subQ38,subQ37,subQ36,subQ35,subQ34,subQ33,subQ32,subQ31,subQ30,subQ29,subQ28,subQ27,subQ26,subQ25,subQ24,subQ23,subQ22,subQ21,subQ20,subQ19,subQ18,subQ17,subQ16,subQ15,subQ14,subQ13,subQ12,subQ11,subQ10,subQ9,subQ8,subQ7,subQ6,subQ5,subQ4,subQ3,subQ2,subQ1,subQ0])],"isStart":false})]}),makeQuery(id+"FArHMtP67R58qOK_1.1.FbB5umPfR1j8SLP_1.5.F8.opExtrude","CAP_FACE",FACE,{"disambiguationData":[OSD([subQ45,subQ44,subQ43,subQ42,subQ41,subQ40,subQ39,subQ38,subQ37,subQ36,subQ35,subQ34,subQ33,subQ32,subQ31,subQ30,subQ29,subQ28,subQ27,subQ26,subQ25,subQ24,subQ23,subQ22,subQ21,subQ20,subQ19,subQ18,subQ17,subQ16,subQ15,subQ14,subQ13,subQ12,subQ11,subQ10,subQ9,subQ8,subQ7,subQ6,subQ5,subQ4,subQ3,subQ2,subQ1,subQ0])],"isStart":false})]});}
            extrude(context, id + "F13", {"entities" : qUnion([Q0]), "operationType" : NewBodyOperationType.REMOVE, "endBound" : BoundingType.UP_TO_SURFACE, "oppositeDirection" : true, "endBoundEntityFace" : qUnion([Q1]), "depth" : 25.4 * mm});
        }
    });
